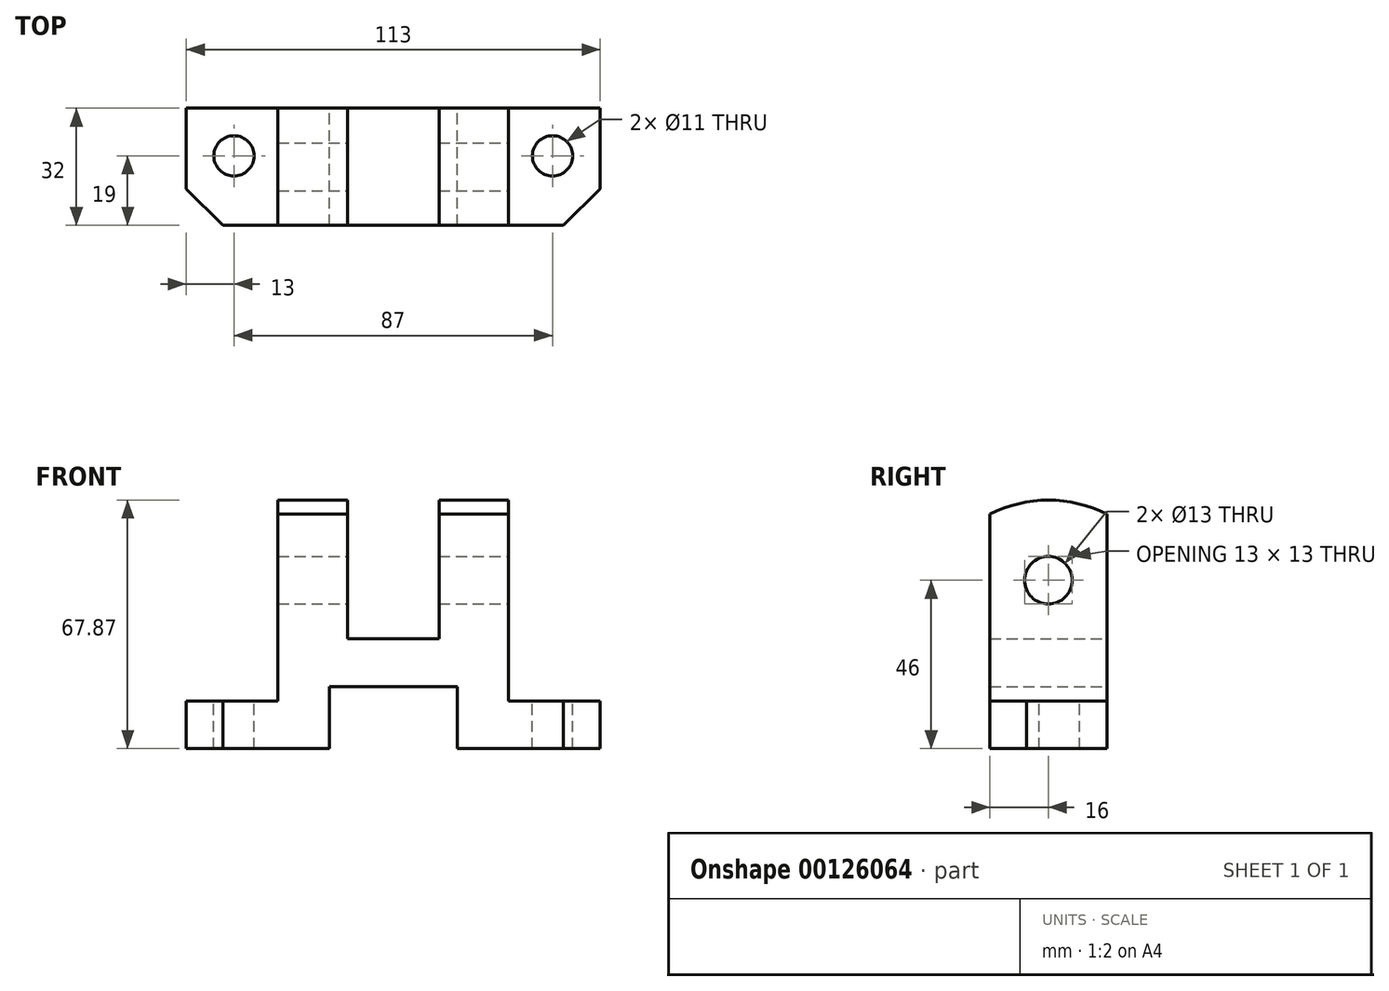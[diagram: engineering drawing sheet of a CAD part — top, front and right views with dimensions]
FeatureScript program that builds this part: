
annotation { "Feature Type Name" : "Feature", "Feature Type Description" : "" }
export const myFeature = defineFeature(function(context is Context, id is Id, definition is map)
    precondition{}
    {
        {
            var Q0;
            Q0=qCreatedBy(makeId("Front.planeOp"),FACE);
            var sketch = newSketch(context, id + "F0", { "sketchPlane" : qUnion([Q0])});
            skLineSegment(sketch, "E0", {"start": v(0, 0) * mm, "end": v(17.5, 0) * mm});
            skLineSegment(sketch, "E1", {"start": v(31.5, 47) * mm, "end": v(31.5, -4) * mm});
            skLineSegment(sketch, "E2", {"start": v(0, 13) * mm, "end": v(12.5, 13) * mm});
            skLineSegment(sketch, "E3", {"start": v(12.5, 13) * mm, "end": v(12.5, 47) * mm});
            skLineSegment(sketch, "E4", {"start": v(12.5, 47) * mm, "end": v(31.5, 47) * mm});
            skLineSegment(sketch, "E5", {"start": v(31.5, -4) * mm, "end": v(56.5, -4) * mm});
            skLineSegment(sketch, "E6", {"start": v(17.5, -17) * mm, "end": v(17.5, 0) * mm});
            skLineSegment(sketch, "E7", {"start": v(17.5, -17) * mm, "end": v(56.5, -17) * mm});
            skLineSegment(sketch, "E8", {"start": v(56.5, -4) * mm, "end": v(56.5, -17) * mm});
            skLineSegment(sketch, "E9.MirrorCS", {"start": v(-31.5, -4) * mm, "end": v(-56.5, -4) * mm});
            skLineSegment(sketch, "E10.MirrorCS", {"start": v(0, 0) * mm, "end": v(-17.5, 0) * mm});
            skLineSegment(sketch, "E11.MirrorCS", {"start": v(-56.5, -4) * mm, "end": v(-56.5, -17) * mm});
            skLineSegment(sketch, "E12.MirrorCS", {"start": v(-17.5, -17) * mm, "end": v(-56.5, -17) * mm});
            skLineSegment(sketch, "E13.MirrorCS", {"start": v(-31.5, 47) * mm, "end": v(-31.5, -4) * mm});
            skLineSegment(sketch, "E14.MirrorCS", {"start": v(-12.5, 13) * mm, "end": v(-12.5, 47) * mm});
            skLineSegment(sketch, "E15.MirrorCS", {"start": v(-12.5, 47) * mm, "end": v(-31.5, 47) * mm});
            skLineSegment(sketch, "E16.MirrorCS", {"start": v(0, 13) * mm, "end": v(-12.5, 13) * mm});
            skLineSegment(sketch, "E17.MirrorCS", {"start": v(-17.5, -17) * mm, "end": v(-17.5, 0) * mm});
            skSolve(sketch);
        }
        {
            var Q0;
            Q0 = qSketchRegion(id + "F0", true);
            extrude(context, id + "F1", {"entities" : qUnion([Q0]), "endBound" : BoundingType.SYMMETRIC, "depth" : 32 * mm});
        }
        {
            var Q0;
            Q0=makeQuery(id+"F1.opExtrude","SWEPT_FACE",FACE,{"disambiguationData":[OSD([sQuery(id+"F0.wireOp",EDGE,"E5")])]});
            var sketch = newSketch(context, id + "F2", { "sketchPlane" : qUnion([Q0])});
            skLineSegment(sketch, "E18", {"start": v(56.5, -16) * mm, "end": v(46.5, -16) * mm});
            skLineSegment(sketch, "E19", {"start": v(46.5, -16) * mm, "end": v(56.5, -6) * mm});
            skLineSegment(sketch, "E20", {"start": v(56.5, -6) * mm, "end": v(56.5, -16) * mm});
            skLineSegment(sketch, "E21.MirrorCS", {"start": v(-56.5, -6) * mm, "end": v(-56.5, -16) * mm});
            skLineSegment(sketch, "E22.MirrorCS", {"start": v(-56.5, -16) * mm, "end": v(-46.5, -16) * mm});
            skLineSegment(sketch, "E23.MirrorCS", {"start": v(-46.5, -16) * mm, "end": v(-56.5, -6) * mm});
            skCircle(sketch, "E24", {"center": v(43.5, 3) * mm, "radius": 5.5 * mm});
            skCircle(sketch, "E25.MirrorC", {"center": v(-43.5, 3) * mm, "radius": 5.5 * mm});
            skSolve(sketch);
        }
        {
            var Q0;
            Q0 = qSketchRegion(id + "F2", true);
            extrude(context, id + "F3", {"entities" : qUnion([Q0]), "operationType" : NewBodyOperationType.REMOVE, "oppositeDirection" : true, "depth" : 25 * mm});
        }
        {
            var Q0;
            Q0=makeQuery(id+"F2.imprint","IMPRINT",FACE,{"disambiguationData":[TD([[makeQuery(id+"F2.imprint","IMPRINT",EDGE,{"derivedFrom":sQuery(id+"F2.wireOp",EDGE,"E24")}),1.0]])]});
            var Q1;
            Q1=makeQuery(id+"F2.imprint","IMPRINT",FACE,{"disambiguationData":[TD([[makeQuery(id+"F2.imprint","IMPRINT",EDGE,{"derivedFrom":sQuery(id+"F2.wireOp",EDGE,"E25.MirrorC")}),-1.0]])]});
            extrude(context, id + "F4", {"entities" : qUnion([Q0, Q1]), "operationType" : NewBodyOperationType.REMOVE, "endBound" : BoundingType.THROUGH_ALL, "oppositeDirection" : true, "depth" : 25 * mm});
        }
        {
            var Q0;
            Q0=makeQuery(id+"F1.opExtrude","SWEPT_FACE",FACE,{"disambiguationData":[OSD([sQuery(id+"F0.wireOp",EDGE,"E1")])]});
            var sketch = newSketch(context, id + "F5", { "sketchPlane" : qUnion([Q0])});
            skCircle(sketch, "E26", {"center": v(0, 29) * mm, "radius": 6.5 * mm});
            skSolve(sketch);
        }
        {
            var Q0;
            Q0=makeQuery(id+"F5.imprint","IMPRINT",FACE,{"disambiguationData":[TD([[makeQuery(id+"F5.imprint","IMPRINT",EDGE,{"derivedFrom":sQuery(id+"F5.wireOp",EDGE,"E26")}),1.0]])]});
            extrude(context, id + "F6", {"entities" : qUnion([Q0]), "operationType" : NewBodyOperationType.REMOVE, "endBound" : BoundingType.THROUGH_ALL, "oppositeDirection" : true, "depth" : 25 * mm});
        }
        {
            var Q0;
            Q0=makeQuery(id+"F1.opExtrude","SWEPT_FACE",FACE,{"disambiguationData":[OSD([sQuery(id+"F0.wireOp",EDGE,"E1")])]});
            var sketch = newSketch(context, id + "F7", { "sketchPlane" : qUnion([Q0])});
            skLineSegment(sketch, "E27", {"start": v(16, -4) * mm, "end": v(22.8, -4) * mm, "construction": true});
            skPoint(sketch, "E27.endSnap0", {"position": v(0, -4) * mm});
            skLineSegment(sketch, "E28", {"start": v(16, 47) * mm, "end": v(19.93, 47) * mm, "construction": true});
            skArc(sketch, "E29", {"start": v(16, 47) * mm, "mid": v(0, 50.87) * mm, "end": v(-16, 47) * mm});
            skLineSegment(sketch, "E30.bottom", {"start": v(-16, 47) * mm, "end": v(16, 47) * mm});
            skLineSegment(sketch, "E31.top", {"start": v(-16, -4) * mm, "end": v(16, -4) * mm});
            skLineSegment(sketch, "E31.left", {"start": v(-16, 47) * mm, "end": v(-16, -4) * mm});
            skLineSegment(sketch, "E31.right", {"start": v(16, 47) * mm, "end": v(16, -4) * mm});
            skSolve(sketch);
        }
        {
            var Q0;
            Q0=makeQuery(id+"F7.imprint","IMPRINT",FACE,{"disambiguationData":[TD([[makeQuery(id+"F7.imprint","IMPRINT",EDGE,{"derivedFrom":sQuery(id+"F7.wireOp",EDGE,"E29")}),1.0]])]});
            extrude(context, id + "F8", {"entities" : qUnion([Q0]), "operationType" : NewBodyOperationType.ADD, "oppositeDirection" : true, "depth" : 19 * mm});
        }
        {
            var Q0;
            Q0=makeQuery(id+"F1.opExtrude","SWEPT_FACE",FACE,{"disambiguationData":[OSD([sQuery(id+"F0.wireOp",EDGE,"E13.MirrorCS")])]});
            var sketch = newSketch(context, id + "F9", { "sketchPlane" : qUnion([Q0])});
            skArc(sketch, "E32", {"start": v(16, 47) * mm, "mid": v(0, 50.87) * mm, "end": v(-16, 47) * mm});
            skLineSegment(sketch, "E33", {"start": v(-16, 47) * mm, "end": v(16, 47) * mm});
            skSolve(sketch);
        }
        {
            var Q0;
            Q0=makeQuery(id+"F9.imprint","IMPRINT",FACE,{"disambiguationData":[TD([[makeQuery(id+"F9.imprint","IMPRINT",EDGE,{"derivedFrom":sQuery(id+"F9.wireOp",EDGE,"E32")}),1.0]])]});
            extrude(context, id + "F10", {"entities" : qUnion([Q0]), "operationType" : NewBodyOperationType.ADD, "oppositeDirection" : true, "depth" : 19 * mm});
        }
    });
